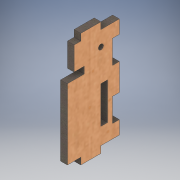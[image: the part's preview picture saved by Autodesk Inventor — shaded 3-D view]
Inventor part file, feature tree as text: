
AUTODESK INVENTOR PART (.ipt)
format: ipt  version: 2019 (Build 230136000, 136)  size: 215,040 bytes
history: native  units: mm
features: extrude x2, sketch x2, other x1
ambient origin geometry x8: Origin, YZ Plane, XZ Plane, XY Plane, X Axis, Y Axis, Z Axis, Center Point
bodies: Body1 (feature_tree)
feature tree (5):
  other  "Твердое тело1"
  extrude  "Выдавливание1"  Depth=4.0mm
  extrude  "Выдавливание2"  Depth=12.0mm
  sketch  "Эскиз2"
  sketch  "Эскиз3"
